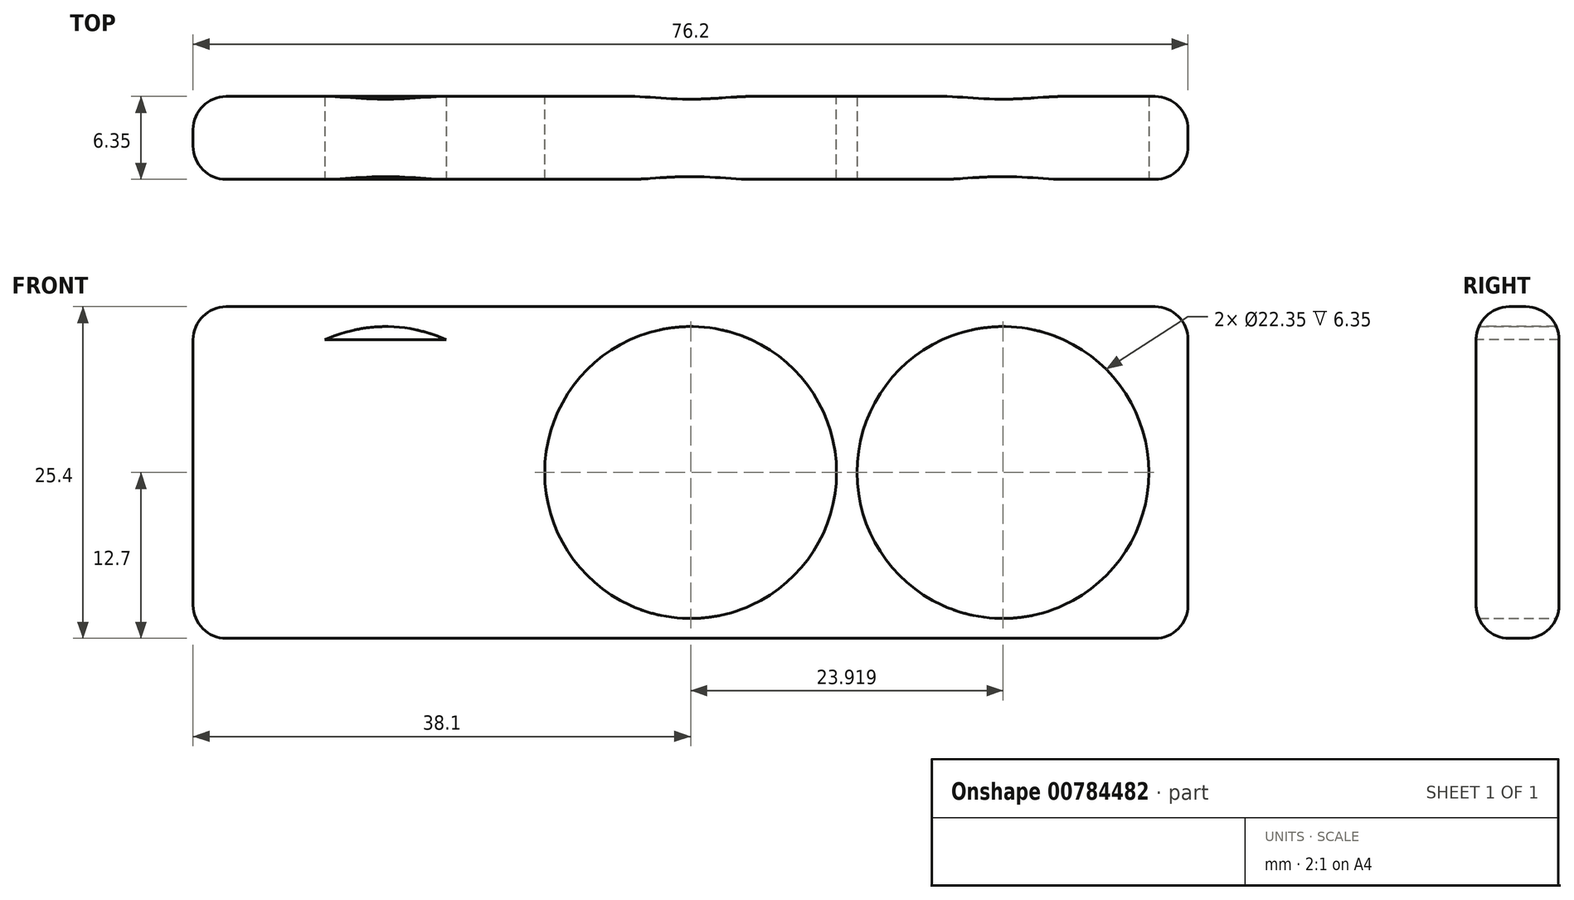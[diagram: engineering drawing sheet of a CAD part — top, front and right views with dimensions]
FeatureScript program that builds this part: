
annotation { "Feature Type Name" : "Feature", "Feature Type Description" : "" }
export const myFeature = defineFeature(function(context is Context, id is Id, definition is map)
    precondition{}
    {
        {
            var Q0;
            Q0=qCreatedBy(makeId("Front.planeOp"),FACE);
            var sketch = newSketch(context, id + "F0", { "sketchPlane" : qUnion([Q0])});
            skLineSegment(sketch, "E0.bottom", {"start": v(38.1, 12.7) * mm, "end": v(-38.1, 12.7) * mm});
            skLineSegment(sketch, "E0.top", {"start": v(38.1, -12.7) * mm, "end": v(-38.1, -12.7) * mm});
            skLineSegment(sketch, "E0.left", {"start": v(38.1, 12.7) * mm, "end": v(38.1, -12.7) * mm});
            skLineSegment(sketch, "E0.right", {"start": v(-38.1, 12.7) * mm, "end": v(-38.1, -12.7) * mm});
            skPoint(sketch, "E0.middle", {"position": v(0, 0) * mm});
            skCircle(sketch, "E1", {"center": v(0, 0) * mm, "radius": 11.18 * mm});
            skSolve(sketch);
        }
        {
            var Q0;
            Q0=makeQuery(id+"F0.imprint","IMPRINT",FACE,{"disambiguationData":[TD([[makeQuery(id+"F0.imprint","IMPRINT",EDGE,{"derivedFrom":sQuery(id+"F0.wireOp",EDGE,"E0.bottom")}),1.0]])]});
            extrude(context, id + "F1", {"entities" : qUnion([Q0]), "depth" : 6.35 * mm, "offsetDistance" : 25.4 * mm});
        }
        {
            var Q0;
            Q0=makeQuery(id+"F1.opExtrude","CAP_EDGE",EDGE,{"disambiguationData":[OSD([sQuery(id+"F0.wireOp",EDGE,"E0.top")])],"isStart":true});
            var Q1;
            Q1=makeQuery(id+"F1.opExtrude","SWEPT_FACE",FACE,{"disambiguationData":[OSD([sQuery(id+"F0.wireOp",EDGE,"E0.top")])]});
            var Q2;
            Q2=makeQuery(id+"F1.opExtrude","SWEPT_EDGE",EDGE,{"disambiguationData":[OSD([sQuery(id+"F0.wireOp",EDGE,"E0.top"),sQuery(id+"F0.wireOp",EDGE,"E0.right")])]});
            var Q3;
            Q3=makeQuery(id+"F1.opExtrude","CAP_EDGE",EDGE,{"disambiguationData":[OSD([sQuery(id+"F0.wireOp",EDGE,"E0.right")])],"isStart":false});
            var Q4;
            Q4=makeQuery(id+"F1.opExtrude","CAP_EDGE",EDGE,{"disambiguationData":[OSD([sQuery(id+"F0.wireOp",EDGE,"E0.right")])],"isStart":true});
            var Q5;
            Q5=makeQuery(id+"F1.opExtrude","CAP_EDGE",EDGE,{"disambiguationData":[OSD([sQuery(id+"F0.wireOp",EDGE,"E0.left")])],"isStart":false});
            var Q6;
            Q6=makeQuery(id+"F1.opExtrude","CAP_EDGE",EDGE,{"disambiguationData":[OSD([sQuery(id+"F0.wireOp",EDGE,"E0.left")])],"isStart":true});
            var Q7;
            Q7=makeQuery(id+"F1.opExtrude","CAP_EDGE",EDGE,{"disambiguationData":[OSD([sQuery(id+"F0.wireOp",EDGE,"E0.bottom")])],"isStart":true});
            var Q8;
            Q8=makeQuery(id+"F1.opExtrude","SWEPT_EDGE",EDGE,{"disambiguationData":[OSD([sQuery(id+"F0.wireOp",EDGE,"E0.bottom"),sQuery(id+"F0.wireOp",EDGE,"E0.left")])]});
            var Q9;
            Q9=makeQuery(id+"F1.opExtrude","SWEPT_EDGE",EDGE,{"disambiguationData":[OSD([sQuery(id+"F0.wireOp",EDGE,"E0.bottom"),sQuery(id+"F0.wireOp",EDGE,"E0.right")])]});
            var Q10;
            Q10=makeQuery(id+"F1.opExtrude","CAP_EDGE",EDGE,{"disambiguationData":[OSD([sQuery(id+"F0.wireOp",EDGE,"E0.bottom")])],"isStart":false});
            fillet(context, id + "F2", {"entities" : qUnion([Q0, Q1, Q2, Q3, Q4, Q5, Q6, Q7, Q8, Q9, Q10]), "radius" : 2.54 * mm, "tangentPropagation" : true, "allowEdgeOverflow" : false});
        }
        {
            var Q0;
            Q0=makeQuery(id+"F2.opFillet","SPLIT",FACE,{"disambiguationData":[OD(1.0)],"derivedFrom":makeQuery(id+"F1.opExtrude","CAP_FACE",FACE,{"disambiguationData":[OSD([sQuery(id+"F0.wireOp",EDGE,"E0.bottom"),sQuery(id+"F0.wireOp",EDGE,"E0.top"),sQuery(id+"F0.wireOp",EDGE,"E0.left"),sQuery(id+"F0.wireOp",EDGE,"E0.right"),sQuery(id+"F0.wireOp",EDGE,"E1")])],"isStart":false})});
            var sketch = newSketch(context, id + "F3", { "sketchPlane" : qUnion([Q0])});
            skCircle(sketch, "E2", {"center": v(-23.36, 0) * mm, "radius": 11.17 * mm});
            skPoint(sketch, "E2.centerSnap0", {"position": v(-35.56, 0) * mm});
            skCircle(sketch, "E3", {"center": v(23.92, 0) * mm, "radius": 11.18 * mm});
            skSolve(sketch);
        }
        {
            var Q0;
            {var subQ0=sQuery(id+"F3.wireOp",EDGE,"E2");var subQ1=sQuery(id+"F0.wireOp",EDGE,"E0.top");var subQ2=sQuery(id+"F0.wireOp",EDGE,"E0.bottom");var subQ3=makeQuery(id+"F1.opExtrude","CAP_FACE",FACE,{"disambiguationData":[OSD([subQ2,subQ1,sQuery(id+"F0.wireOp",EDGE,"E0.left"),sQuery(id+"F0.wireOp",EDGE,"E0.right"),sQuery(id+"F0.wireOp",EDGE,"E1")])],"isStart":false});var subQ4=makeQuery(id+"F2.opFillet","BLEND_EDGE",EDGE,{"disambiguationData":[OD(1.0)],"blendedFrom":[makeQuery(id+"F1.opExtrude","CAP_EDGE",EDGE,{"disambiguationData":[OSD([subQ2])],"isStart":false}),subQ3],"blendedInto":[subQ3]});var subQ5=makeQuery(id+"F3.imprint","INTERSECT",VERTEX,{"disambiguationData":[OD(0.0)],"derivedFrom":[subQ4,subQ0]});Q0=makeQuery(id+"F3.imprint","IMPRINT",FACE,{"disambiguationData":[TD([[makeQuery(id+"F3.imprint","IMPRINT",EDGE,{"disambiguationData":[TD([[subQ5,-1.0]])],"derivedFrom":subQ0}),1.0]])]});}
            var Q1;
            Q1=makeQuery(id+"F3.imprint","IMPRINT",FACE,{"disambiguationData":[TD([[makeQuery(id+"F3.imprint","IMPRINT",EDGE,{"derivedFrom":sQuery(id+"F3.wireOp",EDGE,"E3")}),1.0]])]});
            extrude(context, id + "F4", {"entities" : qUnion([Q0, Q1]), "operationType" : NewBodyOperationType.REMOVE, "oppositeDirection" : true, "depth" : 6.35 * mm, "offsetDistance" : 25.4 * mm});
        }
    });
